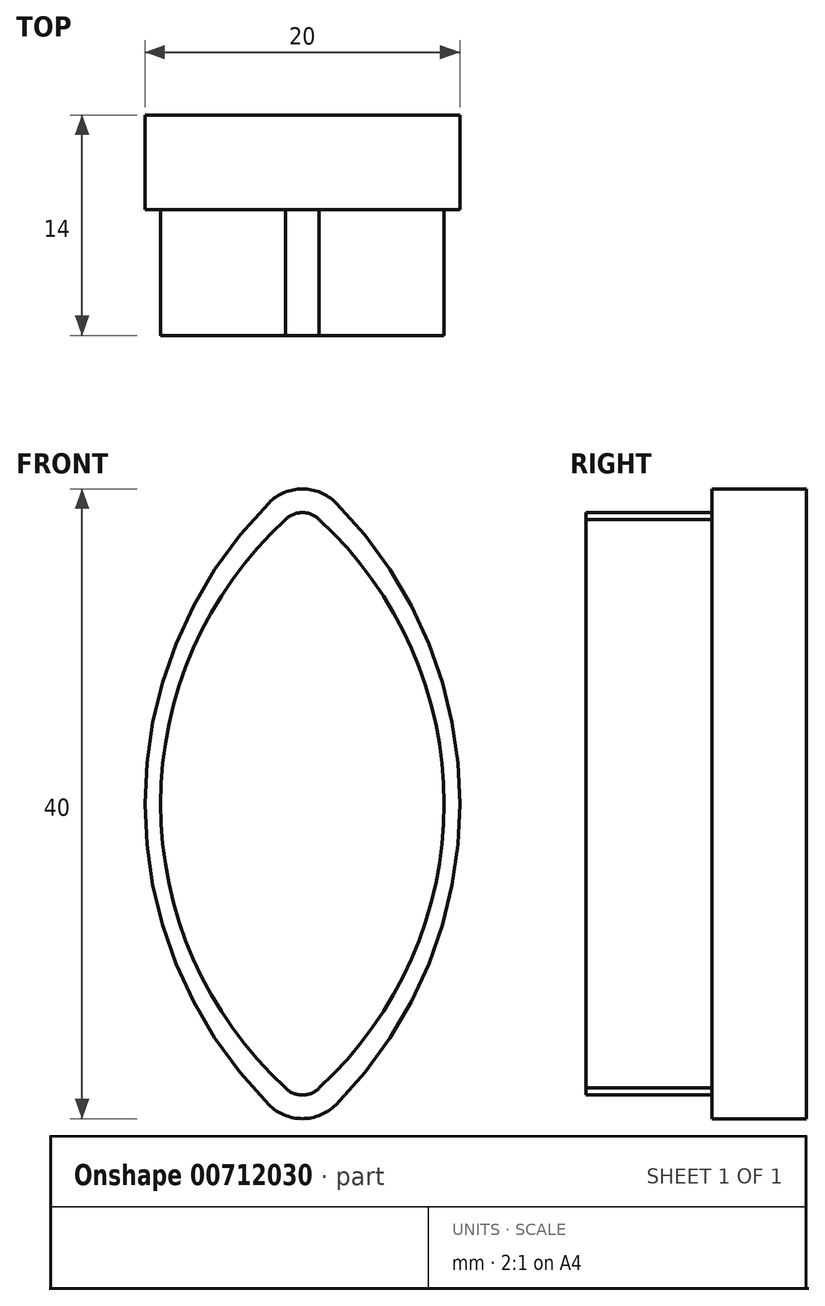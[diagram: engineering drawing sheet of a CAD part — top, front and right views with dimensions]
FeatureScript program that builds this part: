
annotation { "Feature Type Name" : "Feature", "Feature Type Description" : "" }
export const myFeature = defineFeature(function(context is Context, id is Id, definition is map)
    precondition{}
    {
        {
            var Q0;
            Q0=qCreatedBy(makeId("Front.planeOp"),FACE);
            var sketch = newSketch(context, id + "F0", { "sketchPlane" : qUnion([Q0])});
            skLineSegment(sketch, "E0.bottom", {"start": v(0, 0) * mm, "end": v(20, 0) * mm});
            skLineSegment(sketch, "E0.top", {"start": v(0, 40) * mm, "end": v(20, 40) * mm});
            skLineSegment(sketch, "E0.left", {"start": v(0, 0) * mm, "end": v(0, 40) * mm});
            skLineSegment(sketch, "E0.right", {"start": v(20, 0) * mm, "end": v(20, 40) * mm});
            skLineSegment(sketch, "E1", {"start": v(0, 20) * mm, "end": v(20, 20) * mm});
            skLineSegment(sketch, "E2", {"start": v(10, 0) * mm, "end": v(10, 40) * mm});
            skCircle(sketch, "E3", {"center": v(10, 37) * mm, "radius": 3 * mm});
            skCircle(sketch, "E4", {"center": v(10, 3) * mm, "radius": 3 * mm});
            skArc(sketch, "E5", {"start": v(7.87, 39.11) * mm, "mid": v(0, 20) * mm, "end": v(7.87, 0.89) * mm});
            skArc(sketch, "E6", {"start": v(12.13, 0.89) * mm, "mid": v(20, 20) * mm, "end": v(12.13, 39.11) * mm});
            skSolve(sketch);
        }
        {
            var Q0;
            {var subQ1=sQuery(id+"F0.wireOp",EDGE,"E1");var subQ3=sQuery(id+"F0.wireOp",EDGE,"E2");var subQ4=makeQuery(id+"F0.imprint","INTERSECT",VERTEX,{"derivedFrom":[subQ1,subQ3]});Q0=makeQuery(id+"F0.imprint","IMPRINT",FACE,{"disambiguationData":[TD([[makeQuery(id+"F0.imprint","IMPRINT",EDGE,{"disambiguationData":[TD([[subQ4,-1.0]])],"derivedFrom":subQ3}),1.0]])]});}
            var Q1;
            {var subQ1=sQuery(id+"F0.wireOp",EDGE,"E1");var subQ3=sQuery(id+"F0.wireOp",EDGE,"E2");var subQ4=makeQuery(id+"F0.imprint","INTERSECT",VERTEX,{"derivedFrom":[subQ1,subQ3]});Q1=makeQuery(id+"F0.imprint","IMPRINT",FACE,{"disambiguationData":[TD([[makeQuery(id+"F0.imprint","IMPRINT",EDGE,{"disambiguationData":[TD([[subQ4,-1.0]])],"derivedFrom":subQ3}),-1.0]])]});}
            var Q2;
            {var subQ1=sQuery(id+"F0.wireOp",EDGE,"E1");var subQ3=sQuery(id+"F0.wireOp",EDGE,"E2");var subQ4=makeQuery(id+"F0.imprint","INTERSECT",VERTEX,{"derivedFrom":[subQ1,subQ3]});Q2=makeQuery(id+"F0.imprint","IMPRINT",FACE,{"disambiguationData":[TD([[makeQuery(id+"F0.imprint","IMPRINT",EDGE,{"disambiguationData":[TD([[subQ4,1.0]])],"derivedFrom":subQ3}),1.0]])]});}
            var Q3;
            {var subQ1=sQuery(id+"F0.wireOp",EDGE,"E1");var subQ3=sQuery(id+"F0.wireOp",EDGE,"E2");var subQ4=makeQuery(id+"F0.imprint","INTERSECT",VERTEX,{"derivedFrom":[subQ1,subQ3]});Q3=makeQuery(id+"F0.imprint","IMPRINT",FACE,{"disambiguationData":[TD([[makeQuery(id+"F0.imprint","IMPRINT",EDGE,{"disambiguationData":[TD([[subQ4,1.0]])],"derivedFrom":subQ3}),-1.0]])]});}
            var Q4;
            {var subQ0=sQuery(id+"F0.wireOp",EDGE,"E4");var subQ4=makeQuery(id+"F0.imprint","INTERSECT",VERTEX,{"derivedFrom":[subQ0,sQuery(id+"F0.wireOp",EDGE,"E5")]});Q4=makeQuery(id+"F0.imprint","IMPRINT",FACE,{"disambiguationData":[TD([[makeQuery(id+"F0.imprint","IMPRINT",EDGE,{"disambiguationData":[TD([[subQ4,1.0]])],"derivedFrom":subQ0}),1.0]])]});}
            var Q5;
            {var subQ0=sQuery(id+"F0.wireOp",EDGE,"E4");var subQ4=makeQuery(id+"F0.imprint","INTERSECT",VERTEX,{"derivedFrom":[subQ0,sQuery(id+"F0.wireOp",EDGE,"E6")]});Q5=makeQuery(id+"F0.imprint","IMPRINT",FACE,{"disambiguationData":[TD([[makeQuery(id+"F0.imprint","IMPRINT",EDGE,{"disambiguationData":[TD([[subQ4,-1.0]])],"derivedFrom":subQ0}),1.0]])]});}
            var Q6;
            {var subQ0=sQuery(id+"F0.wireOp",EDGE,"E3");var subQ4=makeQuery(id+"F0.imprint","INTERSECT",VERTEX,{"derivedFrom":[subQ0,sQuery(id+"F0.wireOp",EDGE,"E5")]});Q6=makeQuery(id+"F0.imprint","IMPRINT",FACE,{"disambiguationData":[TD([[makeQuery(id+"F0.imprint","IMPRINT",EDGE,{"disambiguationData":[TD([[subQ4,-1.0]])],"derivedFrom":subQ0}),1.0]])]});}
            var Q7;
            {var subQ0=sQuery(id+"F0.wireOp",EDGE,"E3");var subQ4=makeQuery(id+"F0.imprint","INTERSECT",VERTEX,{"derivedFrom":[subQ0,sQuery(id+"F0.wireOp",EDGE,"E6")]});Q7=makeQuery(id+"F0.imprint","IMPRINT",FACE,{"disambiguationData":[TD([[makeQuery(id+"F0.imprint","IMPRINT",EDGE,{"disambiguationData":[TD([[subQ4,1.0]])],"derivedFrom":subQ0}),1.0]])]});}
            extrude(context, id + "F1", {"entities" : qUnion([Q0, Q1, Q2, Q3, Q4, Q5, Q6, Q7]), "depth" : 6 * mm, "offsetDistance" : 25 * mm});
        }
        {
            var Q0;
            Q0=makeQuery(id+"F1.opExtrude","CAP_FACE",FACE,{"disambiguationData":[OSD([sQuery(id+"F0.wireOp",EDGE,"E3"),sQuery(id+"F0.wireOp",EDGE,"E4"),sQuery(id+"F0.wireOp",EDGE,"E5"),sQuery(id+"F0.wireOp",EDGE,"E6")])],"isStart":false});
            var sketch = newSketch(context, id + "F2", { "sketchPlane" : qUnion([Q0])});
            skArc(sketch, "E7.0", {"start": v(11.07, 1.94) * mm, "mid": v(18.5, 20) * mm, "end": v(11.07, 38.06) * mm});
            skArc(sketch, "E7.1", {"start": v(8.93, 1.94) * mm, "mid": v(10, 1.5) * mm, "end": v(11.07, 1.94) * mm});
            skArc(sketch, "E7.2", {"start": v(8.93, 38.06) * mm, "mid": v(1.5, 20) * mm, "end": v(8.93, 1.94) * mm});
            skArc(sketch, "E7.3", {"start": v(11.07, 38.06) * mm, "mid": v(10, 38.5) * mm, "end": v(8.93, 38.06) * mm});
            skLineSegment(sketch, "E8", {"start": v(1.5, 20) * mm, "end": v(2.47, 20) * mm});
            skLineSegment(sketch, "E9", {"start": v(1.5, 20) * mm, "end": v(1, 20) * mm});
            skLineSegment(sketch, "E10", {"start": v(2.47, 20) * mm, "end": v(18.5, 20) * mm});
            skLineSegment(sketch, "E11", {"start": v(18.5, 20) * mm, "end": v(19, 20) * mm});
            skArc(sketch, "E12", {"start": v(8.93, 38.06) * mm, "mid": v(1, 20) * mm, "end": v(8.93, 1.94) * mm});
            skArc(sketch, "E13", {"start": v(11.07, 1.94) * mm, "mid": v(19, 20) * mm, "end": v(11.07, 38.06) * mm});
            skSolve(sketch);
        }
        {
            var Q0;
            Q0=makeQuery(id+"F2.imprint","IMPRINT",FACE,{"disambiguationData":[TD([[makeQuery(id+"F2.imprint","IMPRINT",EDGE,{"derivedFrom":sQuery(id+"F2.wireOp",EDGE,"E7.0")}),1.0]])]});
            var Q1;
            {var subQ3=sQuery(id+"F2.wireOp",EDGE,"E11");Q1=makeQuery(id+"F2.imprint","IMPRINT",FACE,{"disambiguationData":[TD([[makeQuery(id+"F2.imprint","IMPRINT",EDGE,{"derivedFrom":subQ3}),-1.0]])]});}
            var Q2;
            {var subQ3=sQuery(id+"F2.wireOp",EDGE,"E11");Q2=makeQuery(id+"F2.imprint","IMPRINT",FACE,{"disambiguationData":[TD([[makeQuery(id+"F2.imprint","IMPRINT",EDGE,{"derivedFrom":subQ3}),1.0]])]});}
            var Q3;
            {var subQ3=sQuery(id+"F2.wireOp",EDGE,"E9");Q3=makeQuery(id+"F2.imprint","IMPRINT",FACE,{"disambiguationData":[TD([[makeQuery(id+"F2.imprint","IMPRINT",EDGE,{"derivedFrom":subQ3}),1.0]])]});}
            var Q4;
            {var subQ3=sQuery(id+"F2.wireOp",EDGE,"E9");Q4=makeQuery(id+"F2.imprint","IMPRINT",FACE,{"disambiguationData":[TD([[makeQuery(id+"F2.imprint","IMPRINT",EDGE,{"derivedFrom":subQ3}),-1.0]])]});}
            extrude(context, id + "F3", {"entities" : qUnion([Q0, Q1, Q2, Q3, Q4]), "operationType" : NewBodyOperationType.ADD, "depth" : 8 * mm, "offsetDistance" : 25 * mm});
        }
    });
